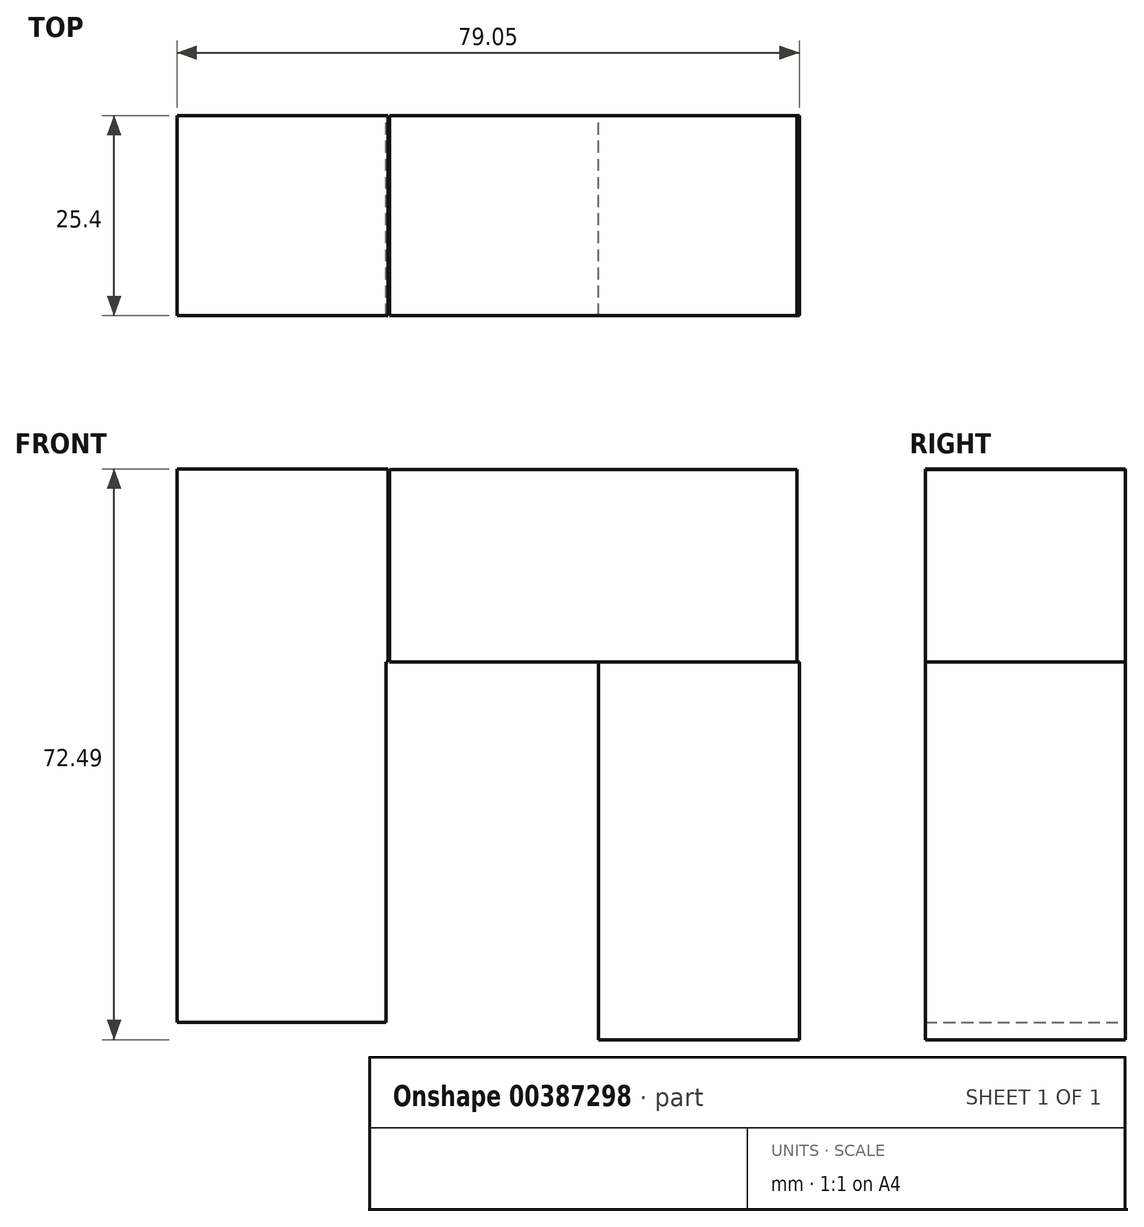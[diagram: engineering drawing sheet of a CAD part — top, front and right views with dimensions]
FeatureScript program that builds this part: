
annotation { "Feature Type Name" : "Feature", "Feature Type Description" : "" }
export const myFeature = defineFeature(function(context is Context, id is Id, definition is map)
    precondition{}
    {
        {
            var Q0;
            Q0=qCreatedBy(makeId("Front.planeOp"),FACE);
            var sketch = newSketch(context, id + "F0", { "sketchPlane" : qUnion([Q0])});
            skLineSegment(sketch, "E0.bottom", {"start": v(0, 0) * mm, "end": v(25.24, 0) * mm});
            skLineSegment(sketch, "E0.top", {"start": v(0, 24.4) * mm, "end": v(25.24, 24.4) * mm});
            skLineSegment(sketch, "E0.left", {"start": v(0, 0) * mm, "end": v(0, 24.4) * mm});
            skLineSegment(sketch, "E0.right", {"start": v(25.24, 0) * mm, "end": v(25.24, 24.4) * mm});
            skLineSegment(sketch, "E1.bottom", {"start": v(0, 0) * mm, "end": v(-26.52, 0) * mm});
            skLineSegment(sketch, "E1.top", {"start": v(0, 24.4) * mm, "end": v(-26.52, 24.4) * mm});
            skLineSegment(sketch, "E1.right", {"start": v(-26.52, 0) * mm, "end": v(-26.52, 24.4) * mm});
            skSolve(sketch);
        }
        {
            var Q0;
            Q0=qCreatedBy(makeId("Front.planeOp"),FACE);
            var sketch = newSketch(context, id + "F1", { "sketchPlane" : qUnion([Q0])});
            skLineSegment(sketch, "E2.bottom", {"start": v(-26.7, 24.48) * mm, "end": v(-53.51, 24.48) * mm});
            skLineSegment(sketch, "E2.top", {"start": v(-26.7, 0) * mm, "end": v(-53.51, 0) * mm});
            skLineSegment(sketch, "E2.left", {"start": v(-26.7, 24.48) * mm, "end": v(-26.7, 0) * mm});
            skLineSegment(sketch, "E2.right", {"start": v(-53.51, 24.48) * mm, "end": v(-53.51, 0) * mm});
            skLineSegment(sketch, "E3.bottom", {"start": v(-53.51, 0) * mm, "end": v(-26.98, 0) * mm});
            skLineSegment(sketch, "E3.top", {"start": v(-53.51, -20.93) * mm, "end": v(-26.98, -20.93) * mm});
            skLineSegment(sketch, "E3.left", {"start": v(-53.51, 0) * mm, "end": v(-53.51, -20.93) * mm});
            skLineSegment(sketch, "E3.right", {"start": v(-26.98, 0) * mm, "end": v(-26.98, -20.93) * mm});
            skLineSegment(sketch, "E4.bottom", {"start": v(-26.98, -20.93) * mm, "end": v(-53.51, -20.93) * mm});
            skLineSegment(sketch, "E4.top", {"start": v(-26.98, -45.82) * mm, "end": v(-53.51, -45.82) * mm});
            skLineSegment(sketch, "E4.left", {"start": v(-26.98, -20.93) * mm, "end": v(-26.98, -45.82) * mm});
            skLineSegment(sketch, "E4.right", {"start": v(-53.51, -20.93) * mm, "end": v(-53.51, -45.82) * mm});
            skLineSegment(sketch, "E5.bottom", {"start": v(25.54, 0) * mm, "end": v(0, 0) * mm});
            skLineSegment(sketch, "E5.top", {"start": v(25.54, -20.93) * mm, "end": v(0, -20.93) * mm});
            skLineSegment(sketch, "E5.left", {"start": v(25.54, 0) * mm, "end": v(25.54, -20.93) * mm});
            skLineSegment(sketch, "E5.right", {"start": v(0, 0) * mm, "end": v(0, -20.93) * mm});
            skLineSegment(sketch, "E6.top", {"start": v(25.54, -48) * mm, "end": v(0, -48) * mm});
            skLineSegment(sketch, "E6.left", {"start": v(25.54, -20.93) * mm, "end": v(25.54, -48) * mm});
            skLineSegment(sketch, "E6.right", {"start": v(0, -20.93) * mm, "end": v(0, -48) * mm});
            skSolve(sketch);
        }
        {
            var Q0;
            Q0 = qSketchRegion(id + "F1", true);
            var Q1;
            Q1=makeQuery(id+"F0.imprint","IMPRINT",FACE,{"disambiguationData":[TD([[makeQuery(id+"F0.imprint","IMPRINT",EDGE,{"derivedFrom":sQuery(id+"F0.wireOp",EDGE,"E1.bottom")}),-1.0]])]});
            var Q2;
            Q2=makeQuery(id+"F0.imprint","IMPRINT",FACE,{"disambiguationData":[TD([[makeQuery(id+"F0.imprint","IMPRINT",EDGE,{"derivedFrom":sQuery(id+"F0.wireOp",EDGE,"E0.bottom")}),1.0]])]});
            extrude(context, id + "F2", {"entities" : qUnion([Q0, Q1, Q2]), "depth" : 25.4 * mm});
        }
    });
